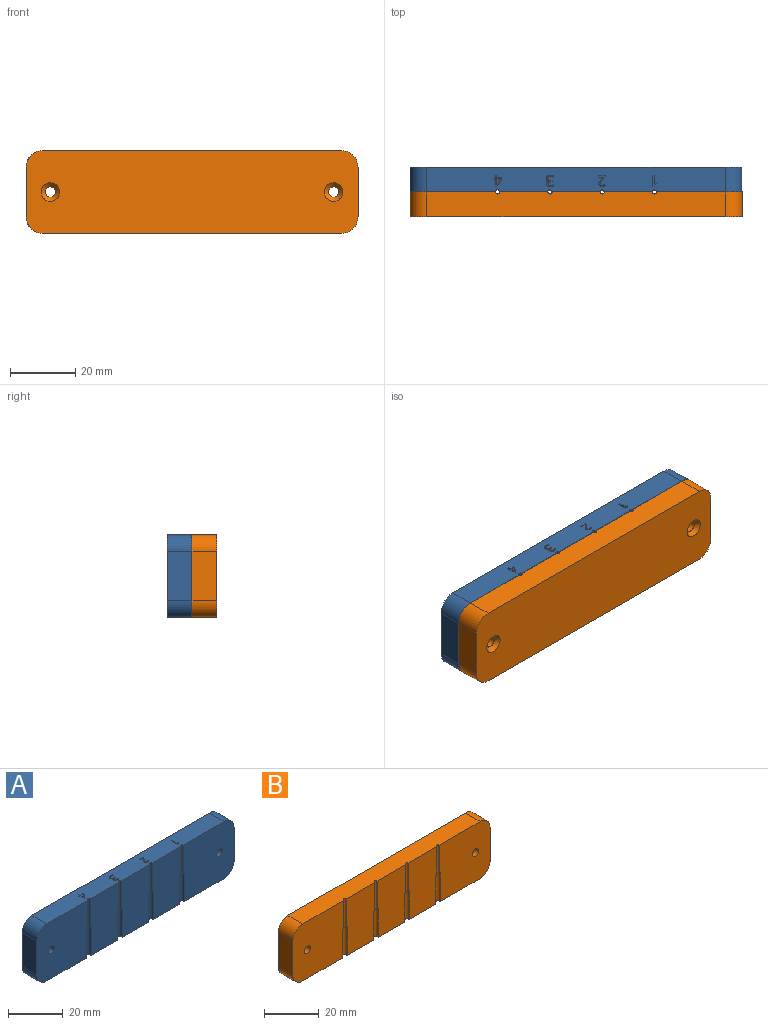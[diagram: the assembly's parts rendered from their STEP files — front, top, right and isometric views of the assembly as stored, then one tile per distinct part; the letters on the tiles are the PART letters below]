
ASSEMBLY  parts=2 mates=1
PART A: 105 faces, bbox 101.6x7.6x25.4 mm
  f0: plane 91.44x7.62mm, normal (0,0,1), area 683.5mm2, adj f1,f2,f3,f4,f10,f15,f17,f18
  f1: plane 25.4x14.73mm, normal (0,-1,0), area 358.1mm2, adj f0,f5,f6,f9,f20,f21,f26,f27
  f2: plane 26.16x25.4mm, normal (0,-1,0), area 637.5mm2, adj f0,f8,f9,f12,f14,f18,f19,f23
  f3: plane 25.4x14.73mm, normal (0,-1,0), area 358.1mm2, adj f0,f7,f8,f9,f22,f23,f24,f25
  f4: plane 25.4x14.73mm, normal (0,-1,0), area 358.1mm2, adj f0,f6,f7,f9,f21,f22,f25,f26
  f5: plane 2.54x1.27mm, normal (0,0,-1), area 1.9mm2, adj f1,f10,f20,f27
  f6: plane 2.54x1.27mm, normal (0,0,-1), area 1.9mm2, adj f1,f4,f21,f26
  f7: plane 2.54x1.27mm, normal (0,0,-1), area 1.9mm2, adj f3,f4,f22,f25
  f8: plane 2.54x1.27mm, normal (0,0,-1), area 1.9mm2, adj f2,f3,f23,f24
  f9: plane 91.44x7.62mm, normal (0,0,-1), area 686.6mm2, adj f1,f2,f3,f4,f10,f15,f16,f19
  f10: plane 26.16x25.4mm, normal (0,-1,0), area 637.5mm2, adj f0,f5,f9,f11,f13,f16,f17,f20
  f11: plane 15.24x7.62mm, normal (1,0,0), area 116.1mm2, adj f10,f15,f16,f17
  f12: cylinder r=1.59mm len=7.62mm, axis (0,1,0), area 76mm2, adj f2,f15
  f13: cylinder r=1.59mm len=7.62mm, axis (0,1,0), area 76mm2, adj f10,f15
  f14: plane 15.24x7.62mm, normal (-1,0,0), area 116.1mm2, adj f2,f15,f18,f19
  f15: plane 101.6x25.4mm, normal (0,1,0), area 2542.7mm2, adj f0,f9,f11,f12,f13,f14,f16,f17
  f16: cylinder r=5.08mm len=7.62mm, axis (0,-1,0), area 60.8mm2, adj f9,f10,f11,f15
  f17: cylinder r=5.08mm len=7.62mm, axis (0,1,0), area 60.8mm2, adj f0,f10,f11,f15
  f18: cylinder r=5.08mm len=7.62mm, axis (0,-1,0), area 60.8mm2, adj f0,f2,f14,f15
  f19: cylinder r=5.08mm len=7.62mm, axis (0,1,0), area 60.8mm2, adj f2,f9,f14,f15
  f20: cylinder r=1.27mm len=12.7mm, axis (0,0,-1), area 50.7mm2, adj f1,f5,f9,f10
  f21: cylinder r=1.27mm len=12.7mm, axis (0,0,-1), area 50.7mm2, adj f1,f4,f6,f9
  f22: cylinder r=1.27mm len=12.7mm, axis (0,0,-1), area 50.7mm2, adj f3,f4,f7,f9
  f23: cylinder r=1.27mm len=12.7mm, axis (0,0,-1), area 50.7mm2, adj f2,f3,f8,f9
  f24: cylinder r=0.64mm len=12.7mm, axis (0,0,1), area 25.3mm2, adj f0,f2,f3,f8
  f25: cylinder r=0.64mm len=12.7mm, axis (0,0,1), area 25.3mm2, adj f0,f3,f4,f7
  f26: cylinder r=0.64mm len=12.7mm, axis (0,0,1), area 25.3mm2, adj f0,f1,f4,f6
  f27: cylinder r=0.64mm len=12.7mm, axis (0,0,1), area 25.3mm2, adj f0,f1,f5,f10
  f28: extruded ~6.35x0.55mm, area 3.7mm2, adj f0,f29,f55,f56
  f29: extruded ~6.35x0.64mm, area 4.6mm2, adj f0,f28,f30,f56
  f30: extruded ~6.35x0.79mm, area 5.3mm2, adj f0,f29,f31,f56
  f31: extruded ~6.35x0.59mm, area 3.8mm2, adj f0,f30,f32,f56
  f32: extruded ~6.35x0.49mm, area 3.6mm2, adj f0,f31,f33,f56
  f33: plane 6.35x0.27mm, normal (-0.8,-0.6,0), area 2.1mm2, adj f0,f32,f34,f56
  f34: extruded ~6.35x0.46mm, area 3.3mm2, adj f0,f33,f35,f56
  f35: extruded ~6.35x0.43mm, area 2.8mm2, adj f0,f34,f36,f56
  f36: extruded ~6.35x0.47mm, area 3.2mm2, adj f0,f35,f37,f56
  f37: extruded ~6.35x0.4mm, area 2.9mm2, adj f0,f36,f38,f56
  f38: extruded ~6.35x0.5mm, area 3.6mm2, adj f0,f37,f39,f56
  f39: extruded ~6.35x0.64mm, area 4.3mm2, adj f0,f38,f40,f56
  f40: plane 6.35x0.35mm, normal (0,1,0), area 2.2mm2, adj f0,f39,f41,f56
  f41: plane 6.35x0.34mm, normal (-1,0,0), area 2.2mm2, adj f0,f40,f42,f56
  f42: plane 6.35x0.34mm, normal (0,-1,0), area 2.2mm2, adj f0,f41,f43,f56
  f43: extruded ~6.35x0.99mm, area 8.5mm2, adj f0,f42,f44,f56
  f44: extruded ~6.35x0.9mm, area 8.3mm2, adj f0,f43,f45,f56
  f45: extruded ~6.35x0.48mm, area 3.1mm2, adj f0,f44,f46,f56
  f46: extruded ~6.35x0.48mm, area 3.3mm2, adj f0,f45,f47,f56
  f47: plane 6.35x0.38mm, normal (-1,0,0), area 2.4mm2, adj f0,f46,f48,f56
  f48: extruded ~6.35x0.45mm, area 3mm2, adj f0,f47,f49,f56
  f49: extruded ~6.35x0.51mm, area 3.2mm2, adj f0,f48,f50,f56
  f50: extruded ~6.35x0.98mm, area 6.6mm2, adj f0,f49,f51,f56
  f51: extruded ~6.35x0.77mm, area 5.5mm2, adj f0,f50,f52,f56
  f52: extruded ~6.35x0.56mm, area 3.9mm2, adj f0,f51,f53,f56
  f53: extruded ~6.35x0.62mm, area 4.4mm2, adj f0,f52,f54,f56
  f54: plane 6.35x0.02mm, normal (1,0,0), area 0.1mm2, adj f0,f53,f55,f56
  f55: extruded ~6.35x0.53mm, area 3.9mm2, adj f0,f28,f54,f56
  f56: plane 3.58x2.28mm, normal (0,0,1), area 2.8mm2, adj f28,f29,f30,f31,f32,f33,f34,f35
  f57: plane 6.35x2.12mm, normal (0,-1,0), area 13.4mm2, adj f0,f58,f76,f77
  f58: plane 6.35x0.34mm, normal (1,0,0), area 2.2mm2, adj f0,f57,f59,f77
  f59: plane 6.35x1.66mm, normal (0,1,0), area 10.5mm2, adj f0,f58,f60,f77
  f60: plane 6.35x0.02mm, normal (1,0,0), area 0.1mm2, adj f0,f59,f61,f77
  f61: plane 6.35x0.71mm, normal (0.7,-0.71,0), area 6.3mm2, adj f0,f60,f62,f77
  f62: extruded ~6.35x0.76mm, area 6.3mm2, adj f0,f61,f63,f77
  f63: extruded ~6.35x0.61mm, area 4mm2, adj f0,f62,f64,f77
  f64: extruded ~6.35x0.62mm, area 4.4mm2, adj f0,f63,f65,f77
  f65: extruded ~6.35x0.71mm, area 4.9mm2, adj f0,f64,f66,f77
  f66: extruded ~6.35x0.97mm, area 6.7mm2, adj f0,f65,f67,f77
  f67: plane 6.35x0.25mm, normal (-0.79,-0.61,0), area 2mm2, adj f0,f66,f68,f77
  f68: extruded ~6.35x0.4mm, area 3mm2, adj f0,f67,f69,f77
  f69: extruded ~6.35x0.38mm, area 2.5mm2, adj f0,f68,f70,f77
  f70: extruded ~6.35x0.43mm, area 3mm2, adj f0,f69,f71,f77
  f71: extruded ~6.35x0.41mm, area 2.9mm2, adj f0,f70,f72,f77
  f72: extruded ~6.35x0.34mm, area 2.2mm2, adj f0,f71,f73,f77
  f73: extruded ~6.35x0.33mm, area 2.4mm2, adj f0,f72,f74,f77
  f74: extruded ~6.35x0.56mm, area 4.8mm2, adj f0,f73,f75,f77
  f75: plane 6.35x0.85mm, normal (-0.71,0.71,0), area 7.6mm2, adj f0,f74,f76,f77
  f76: plane 6.35x0.32mm, normal (-1,0,0), area 2mm2, adj f0,f57,f75,f77
  f77: plane 3.27x2.12mm, normal (0,0,1), area 2.3mm2, adj f57,f58,f59,f60,f61,f62,f63,f64
  f78: plane 6.35x0.53mm, normal (0,-1,0), area 3.4mm2, adj f0,f79,f84,f85
  f79: plane 6.35x3.21mm, normal (1,0,0), area 20.4mm2, adj f0,f78,f80,f85
  f80: plane 6.35x0.53mm, normal (0,1,0), area 3.4mm2, adj f0,f79,f81,f85
  f81: plane 6.35x0.81mm, normal (-0.71,0.71,0), area 7.3mm2, adj f0,f80,f82,f85
  f82: plane 6.35x0.37mm, normal (-0.71,-0.71,0), area 3.4mm2, adj f0,f81,f83,f85
  f83: plane 6.35x0.44mm, normal (0.71,-0.71,0), area 3.9mm2, adj f0,f82,f84,f85
  f84: plane 6.35x2.46mm, normal (-1,0,0), area 15.6mm2, adj f0,f78,f83,f85
  f85: plane 3.21x1.35mm, normal (0,0,1), area 2.2mm2, adj f78,f79,f80,f81,f82,f83,f84
  f86: plane 6.35x1.06mm, normal (-1,0,0), area 6.7mm2, adj f87,f102,f103,f104
  f87: plane 6.35x1.19mm, normal (0,1,0), area 7.5mm2, adj f86,f88,f103,f104
  f88: plane 6.35x1.42mm, normal (0.82,-0.58,0), area 11mm2, adj f87,f89,f103,f104
  f89: extruded ~6.35x0.35mm, area 2.5mm2, adj f88,f90,f103,f104
  f90: plane 6.35x0.02mm, normal (0,-1,0), area 0.1mm2, adj f89,f102,f103,f104
  f91: plane 6.35x0.47mm, normal (0,-1,0), area 3mm2, adj f0,f92,f101,f103
  f92: plane 6.35x0.33mm, normal (1,0,0), area 2.1mm2, adj f0,f91,f93,f103
  f93: plane 6.35x0.47mm, normal (0,1,0), area 3mm2, adj f0,f92,f94,f103
  f94: plane 6.35x2.14mm, normal (1,0,0), area 13.6mm2, adj f0,f93,f95,f103
  f95: plane 6.35x0.38mm, normal (0,1,0), area 2.4mm2, adj f0,f94,f96,f103
  f96: plane 6.35x2.16mm, normal (-0.82,0.57,0), area 16.7mm2, adj f0,f95,f97,f103
  f97: plane 6.35x0.32mm, normal (-1,0,0), area 2mm2, adj f0,f96,f98,f103
  f98: plane 6.35x1.55mm, normal (0,-1,0), area 9.8mm2, adj f0,f97,f99,f103
  f99: plane 6.35x0.73mm, normal (-1,0,0), area 4.6mm2, adj f0,f98,f100,f103
  f100: plane 6.35x0.35mm, normal (0,-1,0), area 2.2mm2, adj f0,f99,f101,f103
  f101: plane 6.35x0.73mm, normal (1,0,0), area 4.6mm2, adj f0,f91,f100,f103
  f102: extruded ~6.35x0.7mm, area 4.5mm2, adj f86,f90,f103,f104
  f103: plane 3.2x2.37mm, normal (0,0,1), area 2.5mm2, adj f86,f87,f88,f89,f90,f91,f92,f93
  f104: plane 1.76x1.21mm, normal (0,0,1), area 1mm2, adj f86,f87,f88,f89,f90,f102
PART B: 30 faces, bbox 101.6x7.6x25.4 mm
  f0: plane 25.4x14.73mm, normal (0,-1,0), area 358.1mm2, adj f4,f5,f6,f9,f20,f21,f26,f27
  f1: plane 26.16x25.4mm, normal (0,-1,0), area 637.5mm2, adj f4,f8,f9,f12,f14,f18,f19,f23
  f2: plane 25.4x14.73mm, normal (0,-1,0), area 358.1mm2, adj f4,f7,f8,f9,f22,f23,f24,f25
  f3: plane 25.4x14.73mm, normal (0,-1,0), area 358.1mm2, adj f4,f6,f7,f9,f21,f22,f25,f26
  f4: plane 91.44x7.62mm, normal (0,0,1), area 694.2mm2, adj f0,f1,f2,f3,f10,f15,f17,f18
  f5: plane 2.54x1.27mm, normal (0,0,-1), area 1.9mm2, adj f0,f10,f20,f27
  f6: plane 2.54x1.27mm, normal (0,0,-1), area 1.9mm2, adj f0,f3,f21,f26
  f7: plane 2.54x1.27mm, normal (0,0,-1), area 1.9mm2, adj f2,f3,f22,f25
  f8: plane 2.54x1.27mm, normal (0,0,-1), area 1.9mm2, adj f1,f2,f23,f24
  f9: plane 91.44x7.62mm, normal (0,0,-1), area 686.6mm2, adj f0,f1,f2,f3,f10,f15,f16,f19
  f10: plane 26.16x25.4mm, normal (0,-1,0), area 637.5mm2, adj f4,f5,f9,f11,f13,f16,f17,f20
  f11: plane 15.24x7.62mm, normal (1,0,0), area 116.1mm2, adj f10,f15,f16,f17
  f12: cylinder r=1.59mm len=6.35mm, axis (0,1,0), area 63.3mm2, adj f1,f29
  f13: cylinder r=1.59mm len=6.35mm, axis (0,1,0), area 63.3mm2, adj f10,f28
  f14: plane 15.24x7.62mm, normal (-1,0,0), area 116.1mm2, adj f1,f15,f18,f19
  f15: plane 101.6x25.4mm, normal (0,1,0), area 2507.2mm2, adj f4,f9,f11,f14,f16,f17,f18,f19
  f16: cylinder r=5.08mm len=7.62mm, axis (0,-1,0), area 60.8mm2, adj f9,f10,f11,f15
  f17: cylinder r=5.08mm len=7.62mm, axis (0,1,0), area 60.8mm2, adj f4,f10,f11,f15
  f18: cylinder r=5.08mm len=7.62mm, axis (0,-1,0), area 60.8mm2, adj f1,f4,f14,f15
  f19: cylinder r=5.08mm len=7.62mm, axis (0,1,0), area 60.8mm2, adj f1,f9,f14,f15
  f20: cylinder r=1.27mm len=12.7mm, axis (0,0,-1), area 50.7mm2, adj f0,f5,f9,f10
  f21: cylinder r=1.27mm len=12.7mm, axis (0,0,-1), area 50.7mm2, adj f0,f3,f6,f9
  f22: cylinder r=1.27mm len=12.7mm, axis (0,0,-1), area 50.7mm2, adj f2,f3,f7,f9
  f23: cylinder r=1.27mm len=12.7mm, axis (0,0,-1), area 50.7mm2, adj f1,f2,f8,f9
  f24: cylinder r=0.64mm len=12.7mm, axis (0,0,1), area 25.3mm2, adj f1,f2,f4,f8
  f25: cylinder r=0.64mm len=12.7mm, axis (0,0,1), area 25.3mm2, adj f2,f3,f4,f7
  f26: cylinder r=0.64mm len=12.7mm, axis (0,0,1), area 25.3mm2, adj f0,f3,f4,f6
  f27: cylinder r=0.64mm len=12.7mm, axis (0,0,1), area 25.3mm2, adj f0,f4,f5,f10
  f28: cone r=2.86mm half-angle=45deg, axis (0,1,0), area 25.1mm2, adj f13,f15
  f29: cone r=2.86mm half-angle=45deg, axis (0,1,0), area 25.1mm2, adj f12,f15
PLACE A t=(49.29,16.68,59.09)mm
PLACE B rot(axis=(0,0,1),180deg) t=(49.37,1.44,59.09)mm
MATE fastened B.f12 <-> A.f13  axis (0,1,0) through (92.71,9.06,59.09)mm
